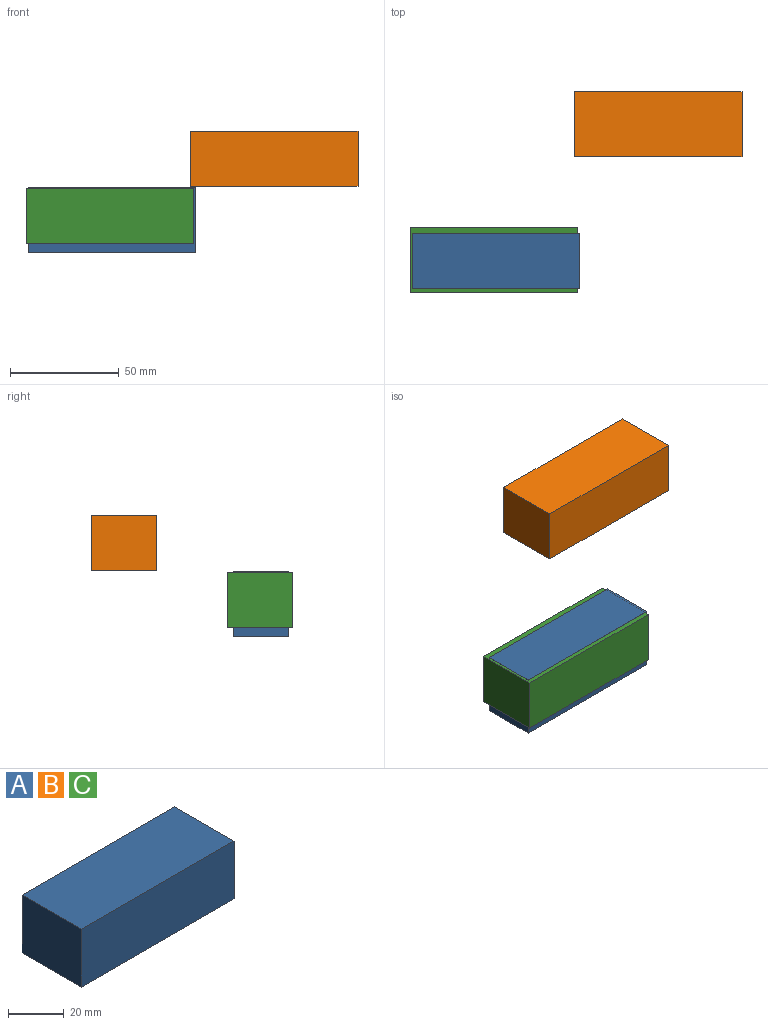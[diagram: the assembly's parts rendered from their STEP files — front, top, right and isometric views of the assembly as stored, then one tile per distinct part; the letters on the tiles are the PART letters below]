
ASSEMBLY  parts=3 mates=1
PART A: 6 faces, bbox 77.3x30x25.4 mm
  f0: plane 77.27x25.4mm, normal (0,1,0), area 1962.6mm2, adj f1,f3,f4,f5
  f1: plane 29.97x25.4mm, normal (-1,0,0), area 761.2mm2, adj f0,f2,f4,f5
  f2: plane 77.27x25.4mm, normal (0,-1,0), area 1962.6mm2, adj f1,f3,f4,f5
  f3: plane 29.97x25.4mm, normal (1,0,0), area 761.2mm2, adj f0,f2,f4,f5
  f4: plane 77.27x29.97mm, normal (0,0,1), area 2315.6mm2, adj f0,f1,f2,f3
  f5: plane 77.27x29.97mm, normal (0,0,-1), area 2315.6mm2, adj f0,f1,f2,f3
PART B: same geometry as A
PART C: same geometry as A
PLACE A rot(axis=(-1,0,0),90deg) t=(-104.03,-41.05,-28.52)mm
PLACE B t=(-29.32,29.4,-18.04)mm
PLACE C rot(axis=(0,0,1),0deg) t=(-104.99,-33.06,-44.4)mm
MATE parallel A.f2 <-> C.f4  axis (0,0,1) through (-8.73,-28.35,-18.67)mm
